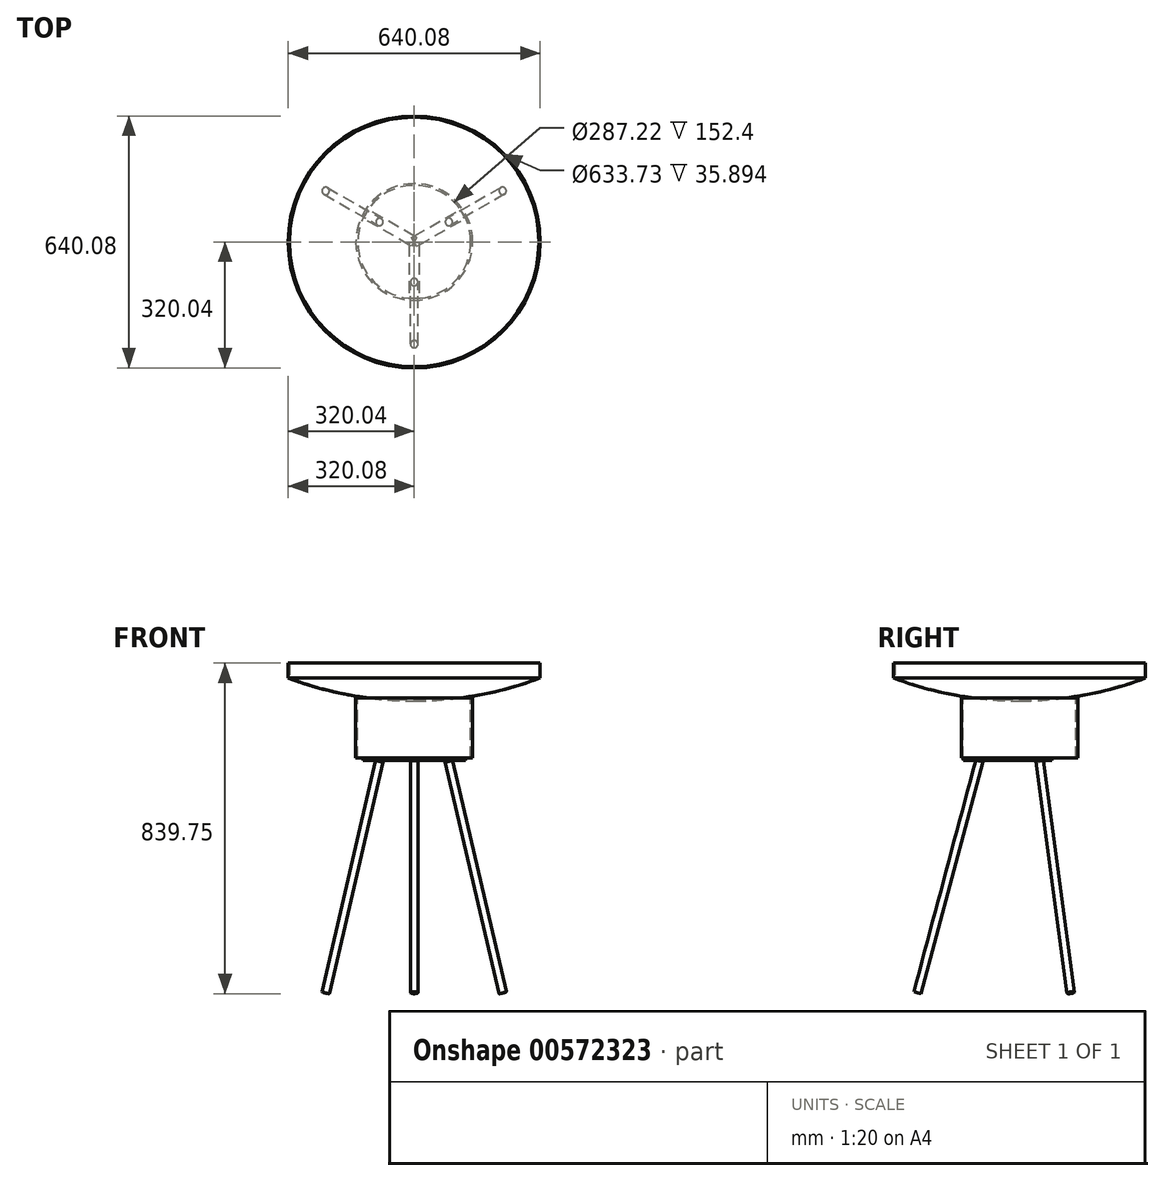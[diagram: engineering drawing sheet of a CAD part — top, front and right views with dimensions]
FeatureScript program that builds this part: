
annotation { "Feature Type Name" : "Feature", "Feature Type Description" : "" }
export const myFeature = defineFeature(function(context is Context, id is Id, definition is map)
    precondition{}
    {
        {
            var Q0;
            Q0=qCreatedBy(makeId("Front.planeOp"),FACE);
            var sketch = newSketch(context, id + "F0", { "sketchPlane" : qUnion([Q0])});
            skArc(sketch, "E0", {"start": v(-320.04, -57.84) * mm, "mid": v(-157.43, -43.26) * mm, "end": v(0, 0) * mm});
            skLineSegment(sketch, "E1", {"start": v(0, 0) * mm, "end": v(0, 38.1) * mm});
            skLineSegment(sketch, "E2.0", {"start": v(-3.18, 2.2) * mm, "end": v(-3.18, 38.1) * mm});
            skArc(sketch, "E2.1", {"start": v(-320.04, -54.66) * mm, "mid": v(-159.08, -40.33) * mm, "end": v(-3.17, 2.2) * mm});
            skLineSegment(sketch, "E3", {"start": v(-3.18, 38.1) * mm, "end": v(0, 38.1) * mm});
            skLineSegment(sketch, "E4", {"start": v(-320.04, -57.84) * mm, "end": v(-320.04, -54.66) * mm});
            skSolve(sketch);
        }
        {
            var Q0;
            Q0 = qSketchRegion(id + "F0", true);
            var Q1;
            Q1=sQuery(id+"F0.wireOp",EDGE,"E4");
            revolve(context, id + "F1", {"surfaceOperationType" : NewSurfaceOperationType.NEW, "entities" : qUnion([Q0]), "axis" : qUnion([Q1]), "revolveType" : RevolveType.FULL});
        }
        {
            var Q0;
            Q0=qCreatedBy(makeId("Top.planeOp"),FACE);
            cPlane(context, id + "F2", {"entities" : qUnion([Q0]), "cplaneType" : CPlaneType.OFFSET, "offset" : 50.8 * mm, "oppositeDirection" : true, "width" : 150 * mm, "height" : 150 * mm});
        }
        {
            var Q0;
            Q0=qCreatedBy(makeId("Right.planeOp"),FACE);
            cPlane(context, id + "F3", {"entities" : qUnion([Q0]), "cplaneType" : CPlaneType.OFFSET, "offset" : 320 * mm, "oppositeDirection" : true, "width" : 150 * mm, "height" : 150 * mm});
        }
        {
            var Q0;
            Q0=qCreatedBy(id+"F2.planeOp",FACE);
            var sketch = newSketch(context, id + "F4", { "sketchPlane" : qUnion([Q0])});
            skCircle(sketch, "E5", {"center": v(-320, 0) * mm, "radius": 148.4 * mm});
            skCircle(sketch, "E6", {"center": v(-320, 0) * mm, "radius": 143.6 * mm});
            skSolve(sketch);
        }
        {
            var Q0;
            Q0 = qSketchRegion(id + "F4", true);
            extrude(context, id + "F5", {"entities" : qUnion([Q0]), "oppositeDirection" : true, "depth" : 152.4 * mm, "offsetDistance" : 25 * mm});
        }
        {
            var Q0;
            Q0=makeQuery(id+"F5.opExtrude","CAP_FACE",FACE,{"disambiguationData":[OSD([sQuery(id+"F4.wireOp",EDGE,"E5"),sQuery(id+"F4.wireOp",EDGE,"E6")])],"isStart":false});
            var sketch = newSketch(context, id + "F6", { "sketchPlane" : qUnion([Q0])});
            skLineSegment(sketch, "E7", {"start": v(-320, 0) * mm, "end": v(-320, 148.4) * mm, "construction": true});
            skLineSegment(sketch, "E8.bottom", {"start": v(-332.7, 0) * mm, "end": v(-307.3, 0) * mm});
            skLineSegment(sketch, "E8.top", {"start": v(-332.7, 143.05) * mm, "end": v(-307.3, 143.05) * mm});
            skLineSegment(sketch, "E8.left", {"start": v(-332.7, 0) * mm, "end": v(-332.7, 143.05) * mm});
            skLineSegment(sketch, "E8.right", {"start": v(-307.3, 0) * mm, "end": v(-307.3, 143.05) * mm});
            skPoint(sketch, "E9.center", {"position": v(0, 0) * mm});
            skLineSegment(sketch, "E10.1.0", {"start": v(-313.65, -11) * mm, "end": v(-437.53, -82.52) * mm});
            skLineSegment(sketch, "E10.1.1", {"start": v(-326.35, 11) * mm, "end": v(-450.23, -60.52) * mm});
            skLineSegment(sketch, "E10.1.2", {"start": v(-437.53, -82.52) * mm, "end": v(-450.23, -60.52) * mm});
            skLineSegment(sketch, "E10.1.3", {"start": v(-313.65, -11) * mm, "end": v(-326.35, 11) * mm});
            skLineSegment(sketch, "E10.2.0", {"start": v(-313.65, 11) * mm, "end": v(-189.77, -60.52) * mm});
            skLineSegment(sketch, "E10.2.1", {"start": v(-326.35, -11) * mm, "end": v(-202.47, -82.52) * mm});
            skLineSegment(sketch, "E10.2.2", {"start": v(-189.77, -60.52) * mm, "end": v(-202.47, -82.52) * mm});
            skLineSegment(sketch, "E10.2.3", {"start": v(-313.65, 11) * mm, "end": v(-326.35, -11) * mm});
            skPoint(sketch, "E10.center", {"position": v(-320, 0) * mm});
            skSolve(sketch);
        }
        {
            var Q0;
            {var subQ1=sQuery(id+"F6.wireOp",EDGE,"E8.top");Q0=makeQuery(id+"F6.imprint","IMPRINT",FACE,{"disambiguationData":[TD([[makeQuery(id+"F6.imprint","IMPRINT",EDGE,{"derivedFrom":subQ1}),-1.0]])]});}
            var Q1;
            {var subQ0=sQuery(id+"F6.wireOp",EDGE,"E10.1.2");Q1=makeQuery(id+"F6.imprint","IMPRINT",FACE,{"disambiguationData":[TD([[makeQuery(id+"F6.imprint","IMPRINT",EDGE,{"derivedFrom":subQ0}),-1.0]])]});}
            var Q2;
            {var subQ9=sQuery(id+"F6.wireOp",EDGE,"E10.2.2");Q2=makeQuery(id+"F6.imprint","IMPRINT",FACE,{"disambiguationData":[TD([[makeQuery(id+"F6.imprint","IMPRINT",EDGE,{"derivedFrom":subQ9}),-1.0]])]});}
            extrude(context, id + "F7", {"entities" : qUnion([Q0, Q1, Q2]), "depth" : 6.35 * mm, "offsetDistance" : 25 * mm});
        }
        {
            var Q0;
            Q0=qCreatedBy(id+"F3.planeOp",FACE);
            var sketch = newSketch(context, id + "F8", { "sketchPlane" : qUnion([Q0])});
            skLineSegment(sketch, "E11", {"start": v(-101.6, -209.55) * mm, "end": v(-259.38, -798.38) * mm});
            skLineSegment(sketch, "E12.0", {"start": v(-111.02, -207.89) * mm, "end": v(-268.8, -796.72) * mm});
            skLineSegment(sketch, "E13", {"start": v(-259.38, -798.38) * mm, "end": v(-268.8, -796.72) * mm});
            skLineSegment(sketch, "E14", {"start": v(-111.02, -207.89) * mm, "end": v(-101.6, -209.55) * mm});
            skLineSegment(sketch, "E15", {"start": v(-101.6, -209.55) * mm, "end": v(-111.02, -207.89) * mm});
            skSolve(sketch);
        }
        {
            var Q0;
            Q0 = qSketchRegion(id + "F8", true);
            var Q1;
            Q1=sQuery(id+"F8.wireOp",EDGE,"E11");
            revolve(context, id + "F9", {"surfaceOperationType" : NewSurfaceOperationType.NEW, "entities" : qUnion([Q0]), "axis" : qUnion([Q1]), "revolveType" : RevolveType.FULL});
        }
        {
            var Q0;
            Q0=makeQuery(id+"F9.opRevolve","SWEPT_BODY",BODY,{"disambiguationData":[OSD([sQuery(id+"F8.wireOp",EDGE,"E11"),sQuery(id+"F8.wireOp",EDGE,"E12.0"),sQuery(id+"F8.wireOp",EDGE,"E13"),sQuery(id+"F8.wireOp",EDGE,"E14")])]});
            var Q1;
            Q1=makeQuery(id+"F1.opRevolve","SWEPT_EDGE",EDGE,{"disambiguationData":[OSD([sQuery(id+"F0.wireOp",EDGE,"E0"),sQuery(id+"F0.wireOp",EDGE,"E1")])]});
            circularPattern(context, id + "F10", {"entities" : qUnion([Q0]), "axis" : qUnion([Q1]), "angle" : 360 * degree, "instanceCount" : 3, "equalSpace" : true});
        }
    });
